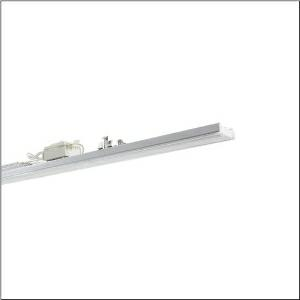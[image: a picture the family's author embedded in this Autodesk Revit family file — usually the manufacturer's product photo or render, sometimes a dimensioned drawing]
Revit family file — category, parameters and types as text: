
# Revit family: licross_11_recessed_mo_51te18dn495g
name_source: partatom
category: Lighting Fixtures
units: mm (PartAtom-declared; Revit-internal decimal feet)

## family parameters
Cut with Voids When Loaded = No
Host = Face
Light Source = No
Part Type = Normal
Room Calculation Point = No
Round Connector Dimension = Use Diameter
Shared = No

## types (1)
- --- (1 x LED, 9950 lm, 56.7 W, 4000K)
    Apparent Load = 57 VA
    CIE Flux Codes = 83 96 99 100 100
    Color Rendering = 80
    Color Temperature = 4000K
    Default Elevation = 1800 mm
    Description = Licross 11 Recessed MO, luminaire insert, of sheet steel, galvanised, coil coated, white, length: 1.500mm, width: 66mm, height: 67mm, LED rated luminous flux: 9.950lm, light colour: 840, SDCM (Standard Deviation of Colour Matching)MacAdam ≤ 2 SDCM (initial), control gear: DALI 2, with plug, 5-pole, with phase selection, mains connection: 220..240V, AC, 50/60Hz, rated input power: 57W, internal wiring halogen-free, primary light control with lens, of plastic, primary optical cover: cover, of PMMA, light emission: direct distribution, primary light characteristic: symmetric, protection rating (complete): IP54, insulation class (complete): insulation class I (protective earthing), certification: CE, ENEC, VDE, UKCA, protection symbol: D if used in an environment with non-conductive dust loads with corresponding accessories, impact resistance: IK06, permissible ambient temperature for indoor applications: -25..+35°C, corresponds to IFS (International Featured Standards) requirements for safety and quality in the food industry, reducing of maximum allowable ambient temperature of 5°C with ceiling mounting, LABS conformity tested according to VDMA 24364:2018-05, The light source and the operating device comply with the requirements of the Ecodesign Regulation (EU) 2019/2020 and are replaceable in accordance with this regulation, packaging unit: 1 piece
    Height = 58 mm
    Lamp = 1 x LED
    Lamp Light Flux = 9950 lm
    Lamp Power = 56.7 W
    Lamp count = 1
    Length = 1500 mm
    Luminous efficacy = 175 lm/W
    Manufacturer = Siteco
    ModVariant = No
    Model = 51TE18DN495G
    Mounting Place = Ceiling
    Mounting Type = Pendant
    Number of Poles = 1
    OnlyDefault = Yes
    Power Factor = 1
    Product Name = Licross 11 Recessed MO
    Product group = luminaire insert | ceiling pendant
    ProductGroupID = 901
    Protection Class = Protection class I
    Protection Degree = IP 54
    RLX_Detail_Level = 1
    RLX_Emergency_Light_Flux = 0 lm
    RLX_Emergency_Type = 0
    RLX_Emergency_Type_DB = No
    RlxData = <blob elided: 24729 chars, md5=2238de9d>
    Socket = socket
    Standby Power = 0 W
    System Light Flux = 9950 lm
    System Power = 57 W
    Type Comments = factory setting: luminous flux: 100 % | dim-lin: 254 | 378 mA
    Type Image = l_1296930.jpg
    URL = http://relux.com
    VarID = @adj_100611
    Voltage = 0 V
    Weight = 0.00 kg
    Width = 66 mm

## geometry (parser evidence)
native form markers: Blend x4, Sweep x12
no freeform markers — native parametric forms only
